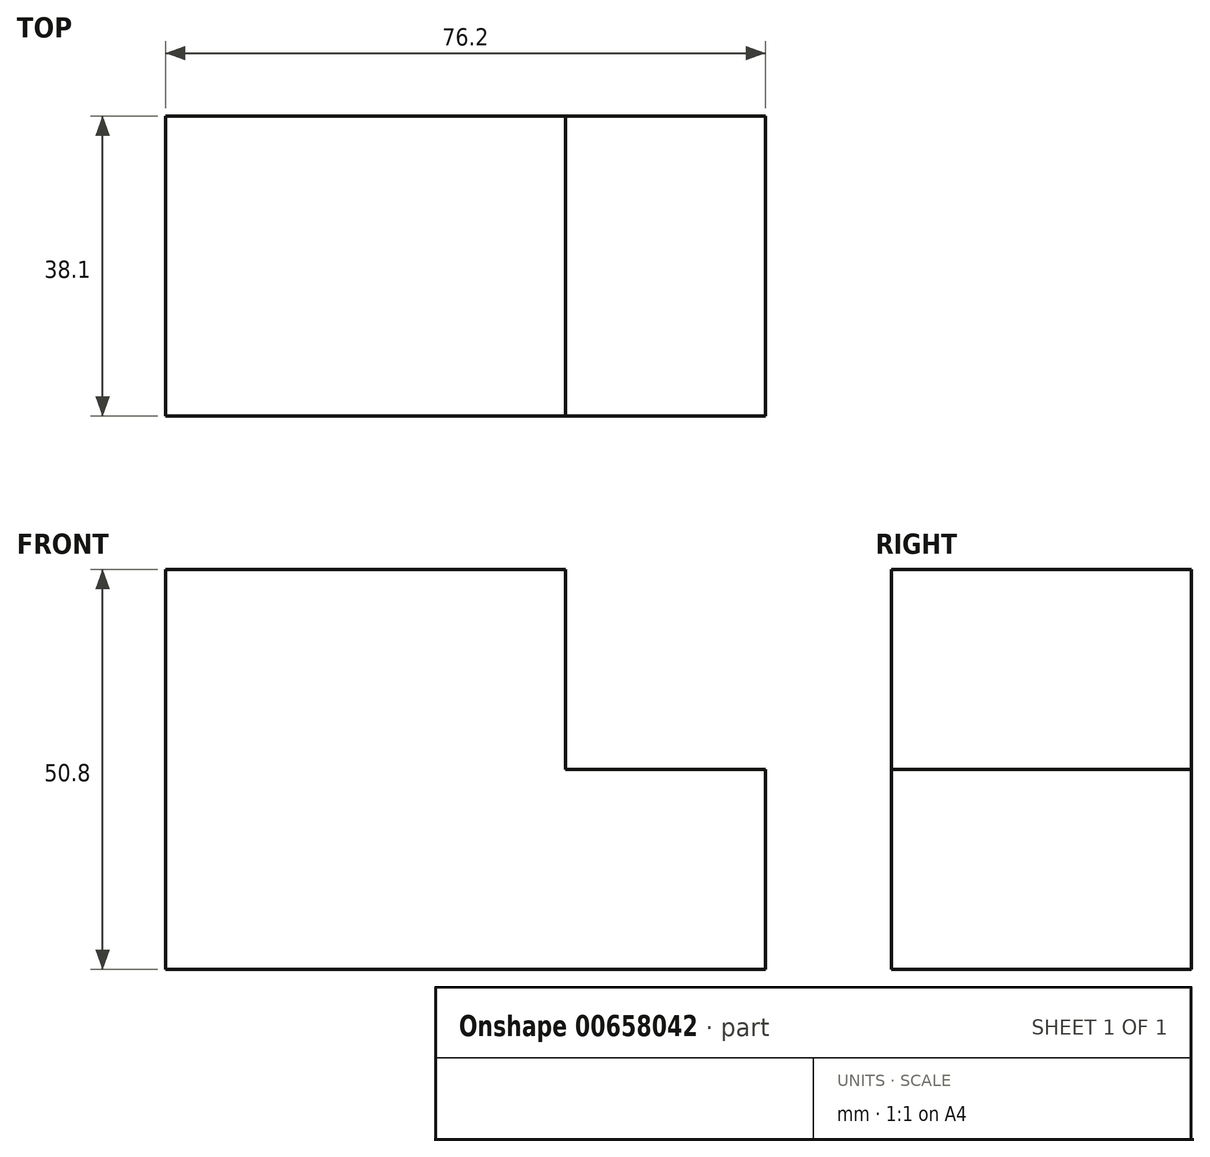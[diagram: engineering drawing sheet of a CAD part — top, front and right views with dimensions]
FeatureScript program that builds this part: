
annotation { "Feature Type Name" : "Feature", "Feature Type Description" : "" }
export const myFeature = defineFeature(function(context is Context, id is Id, definition is map)
    precondition{}
    {
        {
            var Q0;
            Q0=qCreatedBy(makeId("Front.planeOp"),FACE);
            var sketch = newSketch(context, id + "F0", { "sketchPlane" : qUnion([Q0])});
            skLineSegment(sketch, "E0", {"start": v(-32.1, -48.22) * mm, "end": v(44.1, -48.22) * mm});
            skLineSegment(sketch, "E1", {"start": v(44.1, -48.22) * mm, "end": v(44.1, -22.82) * mm});
            skLineSegment(sketch, "E2", {"start": v(44.1, -22.82) * mm, "end": v(18.7, -22.82) * mm});
            skLineSegment(sketch, "E3", {"start": v(18.7, -22.82) * mm, "end": v(18.7, 2.58) * mm});
            skLineSegment(sketch, "E4", {"start": v(18.7, 2.58) * mm, "end": v(-32.1, 2.58) * mm});
            skLineSegment(sketch, "E5", {"start": v(-32.1, 2.58) * mm, "end": v(-32.1, -48.22) * mm});
            skSolve(sketch);
        }
        {
            var Q0;
            Q0=makeQuery(id+"F0.imprint","IMPRINT",FACE,{"disambiguationData":[TD([[makeQuery(id+"F0.imprint","IMPRINT",EDGE,{"derivedFrom":sQuery(id+"F0.wireOp",EDGE,"E0")}),1.0]])]});
            extrude(context, id + "F1", {"entities" : qUnion([Q0]), "depth" : 38.1 * mm, "offsetDistance" : 25.4 * mm});
        }
    });
